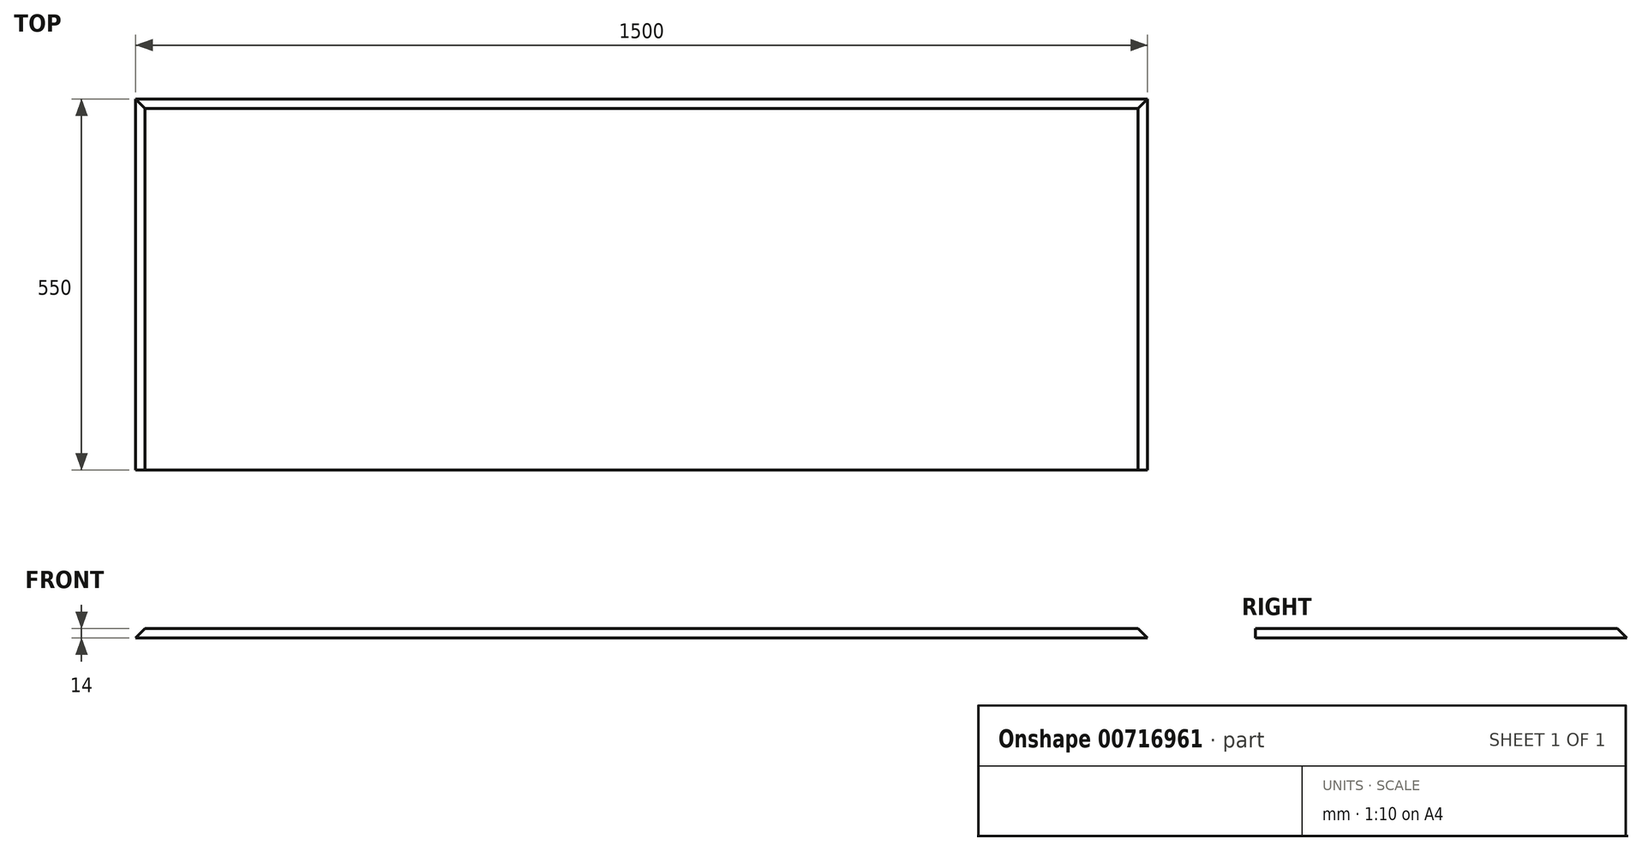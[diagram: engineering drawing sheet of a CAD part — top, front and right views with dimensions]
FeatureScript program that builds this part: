
annotation { "Feature Type Name" : "Feature", "Feature Type Description" : "" }
export const myFeature = defineFeature(function(context is Context, id is Id, definition is map)
    precondition{}
    {
        {
            var Q0;
            Q0=qCreatedBy(makeId("Top.planeOp"),FACE);
            var sketch = newSketch(context, id + "F0", { "sketchPlane" : qUnion([Q0])});
            skLineSegment(sketch, "E0.bottom", {"start": v(750, 275) * mm, "end": v(-750, 275) * mm});
            skLineSegment(sketch, "E0.top", {"start": v(750, -275) * mm, "end": v(-750, -275) * mm});
            skLineSegment(sketch, "E0.left", {"start": v(750, 275) * mm, "end": v(750, -275) * mm});
            skLineSegment(sketch, "E0.right", {"start": v(-750, 275) * mm, "end": v(-750, -275) * mm});
            skPoint(sketch, "E0.middle", {"position": v(0, 0) * mm});
            skSolve(sketch);
        }
        {
            var Q0;
            Q0=makeQuery(id+"F0.imprint","IMPRINT",FACE,{"disambiguationData":[TD([[makeQuery(id+"F0.imprint","IMPRINT",EDGE,{"derivedFrom":sQuery(id+"F0.wireOp",EDGE,"E0.bottom")}),1.0]])]});
            extrude(context, id + "F1", {"entities" : qUnion([Q0]), "depth" : 14 * mm, "offsetDistance" : 25 * mm});
        }
        {
            var Q0;
            Q0=makeQuery(id+"F1.opExtrude","CAP_EDGE",EDGE,{"disambiguationData":[OSD([sQuery(id+"F0.wireOp",EDGE,"E0.right")])],"isStart":false});
            var Q1;
            Q1=makeQuery(id+"F1.opExtrude","CAP_EDGE",EDGE,{"disambiguationData":[OSD([sQuery(id+"F0.wireOp",EDGE,"E0.bottom")])],"isStart":false});
            var Q2;
            Q2=makeQuery(id+"F1.opExtrude","CAP_EDGE",EDGE,{"disambiguationData":[OSD([sQuery(id+"F0.wireOp",EDGE,"E0.left")])],"isStart":false});
            chamfer(context, id + "F2", {"entities" : qUnion([Q0, Q1, Q2]), "width" : 14 * mm, "tangentPropagation" : true});
        }
    });
